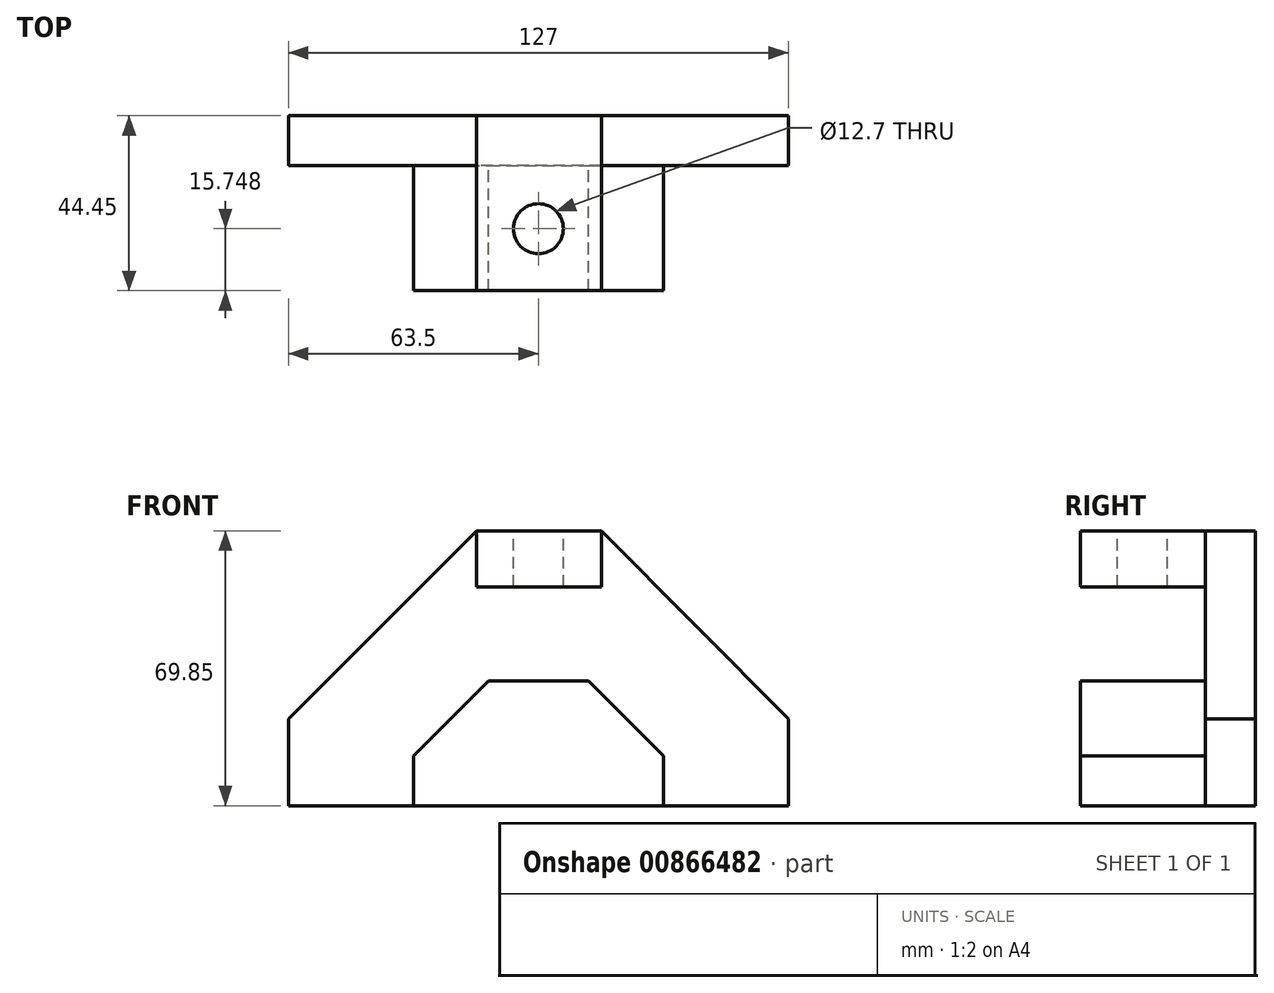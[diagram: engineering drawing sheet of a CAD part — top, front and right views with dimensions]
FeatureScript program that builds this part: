
annotation { "Feature Type Name" : "Feature", "Feature Type Description" : "" }
export const myFeature = defineFeature(function(context is Context, id is Id, definition is map)
    precondition{}
    {
        {
            var Q0;
            Q0=qCreatedBy(makeId("Front.planeOp"),FACE);
            var sketch = newSketch(context, id + "F0", { "sketchPlane" : qUnion([Q0])});
            skLineSegment(sketch, "E0", {"start": v(0, 0) * mm, "end": v(-19.05, 0) * mm});
            skLineSegment(sketch, "E1", {"start": v(0, 0) * mm, "end": v(25.4, 0) * mm});
            skLineSegment(sketch, "E2", {"start": v(25.4, 0) * mm, "end": v(44.45, 0) * mm});
            skLineSegment(sketch, "E3", {"start": v(44.45, 0) * mm, "end": v(44.45, 12.7) * mm});
            skLineSegment(sketch, "E4", {"start": v(-19.05, 0) * mm, "end": v(-19.05, 12.7) * mm});
            skLineSegment(sketch, "E5", {"start": v(-19.05, 12.7) * mm, "end": v(0, 31.75) * mm});
            skLineSegment(sketch, "E6", {"start": v(0, 31.75) * mm, "end": v(25.4, 31.75) * mm});
            skLineSegment(sketch, "E7", {"start": v(25.4, 31.75) * mm, "end": v(44.45, 12.7) * mm});
            skLineSegment(sketch, "E8", {"start": v(44.45, 0) * mm, "end": v(76.2, 0) * mm});
            skLineSegment(sketch, "E9", {"start": v(-19.05, 0) * mm, "end": v(-50.8, 0) * mm});
            skLineSegment(sketch, "E10", {"start": v(-50.8, 0) * mm, "end": v(-50.8, 22.1) * mm});
            skLineSegment(sketch, "E11", {"start": v(-50.8, 22.1) * mm, "end": v(-3.05, 69.85) * mm});
            skLineSegment(sketch, "E12", {"start": v(-3.05, 69.85) * mm, "end": v(28.7, 69.85) * mm});
            skLineSegment(sketch, "E13", {"start": v(76.2, 0) * mm, "end": v(76.2, 22.1) * mm});
            skLineSegment(sketch, "E14", {"start": v(28.7, 69.85) * mm, "end": v(76.2, 22.1) * mm});
            skLineSegment(sketch, "E15", {"start": v(28.7, 69.85) * mm, "end": v(28.7, 55.63) * mm});
            skLineSegment(sketch, "E16", {"start": v(28.7, 55.63) * mm, "end": v(-3.05, 55.63) * mm});
            skLineSegment(sketch, "E17", {"start": v(-3.05, 69.85) * mm, "end": v(-3.05, 55.63) * mm});
            skSolve(sketch);
        }
        {
            var Q0;
            Q0=makeQuery(id+"F0.imprint","IMPRINT",FACE,{"disambiguationData":[TD([[makeQuery(id+"F0.imprint","IMPRINT",EDGE,{"derivedFrom":sQuery(id+"F0.wireOp",EDGE,"E0")}),-1.0]])]});
            extrude(context, id + "F1", {"entities" : qUnion([Q0]), "depth" : 31.75 * mm, "offsetDistance" : 25.4 * mm});
        }
        {
            var Q0;
            Q0=makeQuery(id+"F0.imprint","IMPRINT",FACE,{"disambiguationData":[TD([[makeQuery(id+"F0.imprint","IMPRINT",EDGE,{"derivedFrom":sQuery(id+"F0.wireOp",EDGE,"E3")}),-1.0]])]});
            extrude(context, id + "F2", {"entities" : qUnion([Q0]), "oppositeDirection" : true, "depth" : 12.7 * mm, "offsetDistance" : 25.4 * mm});
        }
        {
            var Q0;
            Q0=makeQuery(id+"F0.imprint","IMPRINT",FACE,{"disambiguationData":[TD([[makeQuery(id+"F0.imprint","IMPRINT",EDGE,{"derivedFrom":sQuery(id+"F0.wireOp",EDGE,"E12")}),-1.0]])]});
            extrude(context, id + "F3", {"entities" : qUnion([Q0]), "operationType" : NewBodyOperationType.ADD, "depth" : 31.75 * mm, "offsetDistance" : 25.4 * mm, "hasSecondDirection" : true, "secondDirectionOppositeDirection" : true, "secondDirectionDepth" : 12.7 * mm});
        }
        {
            var Q0;
            Q0=makeQuery(id+"F1.opExtrude","CAP_FACE",FACE,{"disambiguationData":[OSD([sQuery(id+"F0.wireOp",EDGE,"E0"),sQuery(id+"F0.wireOp",EDGE,"E1"),sQuery(id+"F0.wireOp",EDGE,"E2"),sQuery(id+"F0.wireOp",EDGE,"E3"),sQuery(id+"F0.wireOp",EDGE,"E4"),sQuery(id+"F0.wireOp",EDGE,"E5"),sQuery(id+"F0.wireOp",EDGE,"E6"),sQuery(id+"F0.wireOp",EDGE,"E7")])],"isStart":true});
            var Q1;
            {var subQ0=sQuery(id+"F0.wireOp",EDGE,"E17");var subQ1=sQuery(id+"F0.wireOp",EDGE,"E16");var subQ2=sQuery(id+"F0.wireOp",EDGE,"E15");Q1=makeQuery(id+"F3.boolean.opBoolean","MERGE",FACE,{"derivedFrom":[makeQuery(id+"F2.opExtrude","CAP_FACE",FACE,{"disambiguationData":[OSD([sQuery(id+"F0.wireOp",EDGE,"E3"),sQuery(id+"F0.wireOp",EDGE,"E4"),sQuery(id+"F0.wireOp",EDGE,"E5"),sQuery(id+"F0.wireOp",EDGE,"E6"),sQuery(id+"F0.wireOp",EDGE,"E7"),sQuery(id+"F0.wireOp",EDGE,"E8"),sQuery(id+"F0.wireOp",EDGE,"E9"),sQuery(id+"F0.wireOp",EDGE,"E10"),sQuery(id+"F0.wireOp",EDGE,"E11"),sQuery(id+"F0.wireOp",EDGE,"E13"),sQuery(id+"F0.wireOp",EDGE,"E14"),subQ2,subQ1,subQ0])],"isStart":false}),makeQuery(id+"F3.opExtrude","CAP_FACE",FACE,{"disambiguationData":[OSD([sQuery(id+"F0.wireOp",EDGE,"E12"),subQ2,subQ1,subQ0])],"isStart":true})]});}
            extrude(context, id + "F4", {"entities" : qUnion([Q0]), "operationType" : NewBodyOperationType.ADD, "endBound" : BoundingType.UP_TO_SURFACE, "depth" : 25.4 * mm, "endBoundEntityFace" : qUnion([Q1]), "offsetDistance" : 25.4 * mm});
        }
        {
            var Q0;
            Q0=makeQuery(id+"F3.opExtrude","SWEPT_FACE",FACE,{"disambiguationData":[OSD([sQuery(id+"F0.wireOp",EDGE,"E12")])]});
            var sketch = newSketch(context, id + "F5", { "sketchPlane" : qUnion([Q0])});
            skCircle(sketch, "E18", {"center": v(12.7, -16) * mm, "radius": 6.35 * mm});
            skSolve(sketch);
        }
        {
            var Q0;
            Q0=makeQuery(id+"F5.imprint","IMPRINT",FACE,{"disambiguationData":[TD([[makeQuery(id+"F5.imprint","IMPRINT",EDGE,{"derivedFrom":sQuery(id+"F5.wireOp",EDGE,"E18")}),1.0]])]});
            extrude(context, id + "F6", {"entities" : qUnion([Q0]), "operationType" : NewBodyOperationType.REMOVE, "oppositeDirection" : true, "depth" : 14.22 * mm, "offsetDistance" : 25.4 * mm});
        }
    });
